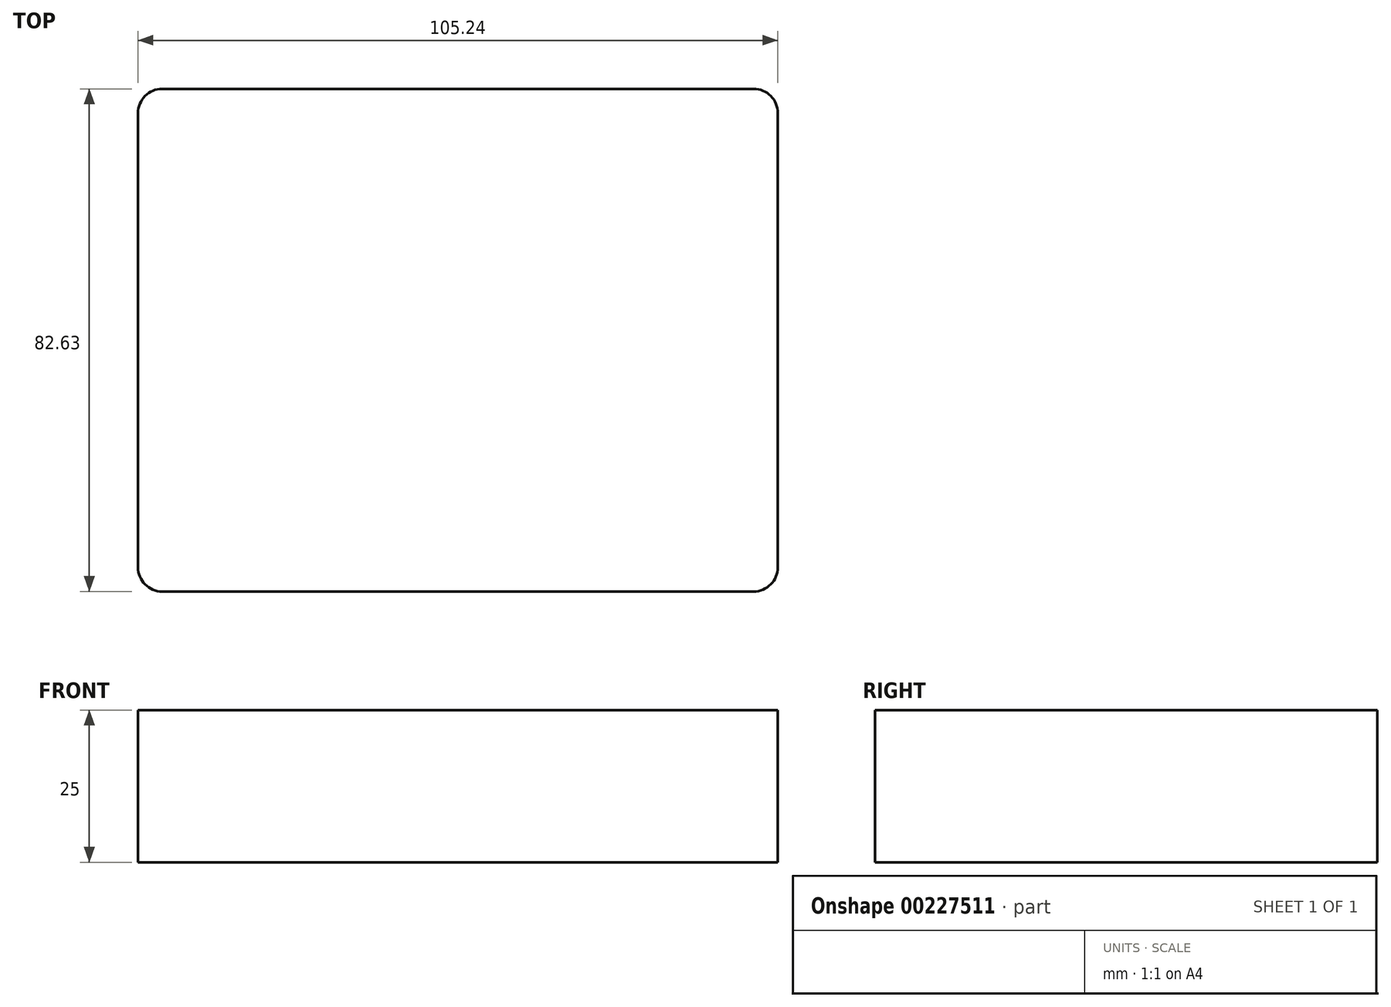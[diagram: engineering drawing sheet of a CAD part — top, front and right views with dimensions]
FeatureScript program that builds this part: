
annotation { "Feature Type Name" : "Feature", "Feature Type Description" : "" }
export const myFeature = defineFeature(function(context is Context, id is Id, definition is map)
    precondition{}
    {
        {
            var Q0;
            Q0=qCreatedBy(makeId("Top.planeOp"),FACE);
            var sketch = newSketch(context, id + "F0", { "sketchPlane" : qUnion([Q0])});
            skLineSegment(sketch, "E0.bottom", {"start": v(-48.62, 38.09) * mm, "end": v(0, 38.09) * mm});
            skLineSegment(sketch, "E0.top", {"start": v(-48.62, -44.54) * mm, "end": v(0, -44.54) * mm});
            skLineSegment(sketch, "E0.left", {"start": v(-52.62, 34.09) * mm, "end": v(-52.62, -40.54) * mm});
            skLineSegment(sketch, "E0.right", {"start": v(0, 38.09) * mm, "end": v(0, -44.54) * mm});
            skLineSegment(sketch, "E1.MirrorCS", {"start": v(48.62, 38.09) * mm, "end": v(0, 38.09) * mm});
            skLineSegment(sketch, "E2.MirrorCS", {"start": v(52.62, 34.09) * mm, "end": v(52.62, -40.54) * mm});
            skLineSegment(sketch, "E3.MirrorCS", {"start": v(48.62, -44.54) * mm, "end": v(0, -44.54) * mm});
            skPoint(sketch, "E4.visualSharp", {"position": v(-52.62, 38.09) * mm});
            skArc(sketch, "E4.filletArc", {"start": v(-48.62, 38.09) * mm, "mid": v(-51.45, 36.91) * mm, "end": v(-52.62, 34.09) * mm});
            skPoint(sketch, "E5.visualSharp", {"position": v(-52.62, -44.54) * mm});
            skArc(sketch, "E5.filletArc", {"start": v(-52.62, -40.54) * mm, "mid": v(-51.45, -43.37) * mm, "end": v(-48.62, -44.54) * mm});
            skPoint(sketch, "E6.visualSharp", {"position": v(52.62, 38.09) * mm});
            skArc(sketch, "E6.filletArc", {"start": v(52.62, 34.09) * mm, "mid": v(51.45, 36.91) * mm, "end": v(48.62, 38.09) * mm});
            skPoint(sketch, "E7.visualSharp", {"position": v(52.62, -44.54) * mm});
            skArc(sketch, "E7.filletArc", {"start": v(48.62, -44.54) * mm, "mid": v(51.45, -43.37) * mm, "end": v(52.62, -40.54) * mm});
            skSolve(sketch);
        }
        {
            var Q0;
            Q0=makeQuery(id+"F0.imprint","IMPRINT",FACE,{"disambiguationData":[TD([[makeQuery(id+"F0.imprint","IMPRINT",EDGE,{"derivedFrom":sQuery(id+"F0.wireOp",EDGE,"E0.bottom")}),-1.0]])]});
            var Q1;
            Q1=makeQuery(id+"F0.imprint","IMPRINT",FACE,{"disambiguationData":[TD([[makeQuery(id+"F0.imprint","IMPRINT",EDGE,{"derivedFrom":sQuery(id+"F0.wireOp",EDGE,"E0.right")}),1.0]])]});
            extrude(context, id + "F1", {"entities" : qUnion([Q0, Q1]), "depth" : 25 * mm});
        }
    });
